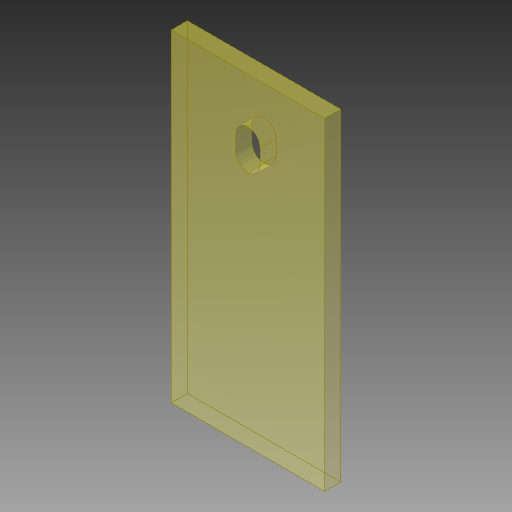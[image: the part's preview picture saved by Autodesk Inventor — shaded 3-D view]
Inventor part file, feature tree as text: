
AUTODESK INVENTOR PART (.ipt)
format: ipt  version: 2018.1 (Build 221171000, 171)  size: 109,056 bytes
history: native  units: mm
features: other x4, extrude x2, sketch x2, reference x2
ambient origin geometry x8: Origin, YZ Plane, XZ Plane, XY Plane, X Axis, Y Axis, Z Axis, Center Point
bodies: Solid1 (feature_tree)
feature tree (10):
  parser-record x2  (decoder bookkeeping rows leaked as tree rows — omitted from the tree; the rows remain in map.json)
  extrude  "Extrusion1"  Depth=400.0mm
  extrude  "Extrusion2"  TaperAngle=0.0deg  [1 undecoded]
  sketch  "Sketch1"  dims[d0=190.0mm d1=400.0mm]
  sketch  "Sketch2"  dims[d2=20.0mm d3=0.0mm d4=15.0mm d5=15.0mm d6=180.0deg d7=20.0mm d8=0.0mm]
  reference  "Reference1"
  reference  "Reference2"
  other  "load cell_assembly.iam"
  other  "platform_bottom:1"
note: 1 required parameter value undecoded (feature->parameter linkage not recoverable at this tier; creation-order binding heuristic only, values carry confidence <= 0.55)
note: 2 file-system paths scrubbed to <path> (originals preserved in map.json)
